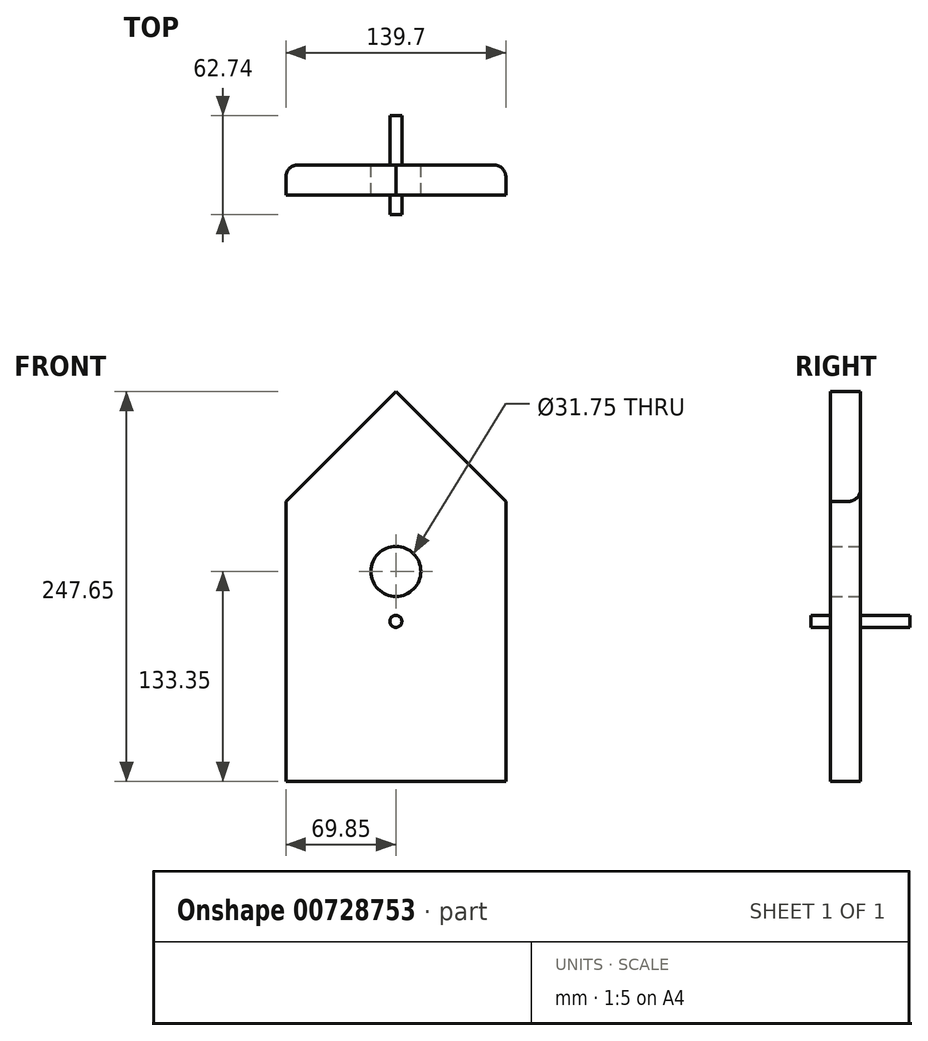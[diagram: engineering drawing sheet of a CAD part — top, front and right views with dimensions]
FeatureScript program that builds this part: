
annotation { "Feature Type Name" : "Feature", "Feature Type Description" : "" }
export const myFeature = defineFeature(function(context is Context, id is Id, definition is map)
    precondition{}
    {
        {
            var Q0;
            Q0=qCreatedBy(makeId("Front.planeOp"),FACE);
            var sketch = newSketch(context, id + "F0", { "sketchPlane" : qUnion([Q0])});
            skLineSegment(sketch, "E0.bottom", {"start": v(69.85, -88.9) * mm, "end": v(-69.85, -88.9) * mm});
            skLineSegment(sketch, "E0.left", {"start": v(69.85, -88.9) * mm, "end": v(69.85, 88.9) * mm});
            skLineSegment(sketch, "E0.right", {"start": v(-69.85, -88.9) * mm, "end": v(-69.85, 88.9) * mm});
            skPoint(sketch, "E0.middle", {"position": v(0, 0) * mm});
            skLineSegment(sketch, "E1", {"start": v(-69.85, 88.9) * mm, "end": v(0, 158.75) * mm});
            skLineSegment(sketch, "E2", {"start": v(0, 158.75) * mm, "end": v(69.85, 88.9) * mm});
            skCircle(sketch, "E3", {"center": v(0, 44.45) * mm, "radius": 15.88 * mm});
            skCircle(sketch, "E4", {"center": v(0, 12.7) * mm, "radius": 3.81 * mm});
            skSolve(sketch);
        }
        {
            var Q0;
            Q0 = qSketchRegion(id + "F0", true);
            extrude(context, id + "F1", {"entities" : qUnion([Q0]), "depth" : 19.05 * mm, "offsetDistance" : 25.4 * mm});
        }
        {
            var Q0;
            Q0=makeQuery(id+"F0.imprint","IMPRINT",FACE,{"disambiguationData":[TD([[makeQuery(id+"F0.imprint","IMPRINT",EDGE,{"derivedFrom":sQuery(id+"F0.wireOp",EDGE,"E4")}),1.0]])]});
            extrude(context, id + "F2", {"entities" : qUnion([Q0]), "operationType" : NewBodyOperationType.ADD, "endBound" : BoundingType.SYMMETRIC, "depth" : 62.74 * mm, "offsetDistance" : 25.4 * mm});
        }
        {
            var Q0;
            Q0=makeQuery(id+"F1.opExtrude","CAP_EDGE",EDGE,{"disambiguationData":[OSD([sQuery(id+"F0.wireOp",EDGE,"E0.left")])],"isStart":true});
            fillet(context, id + "F3", {"entities" : qUnion([Q0]), "radius" : 7.62 * mm, "tangentPropagation" : true, "allowEdgeOverflow" : false});
        }
        {
            var Q0;
            Q0=makeQuery(id+"F1.opExtrude","CAP_EDGE",EDGE,{"disambiguationData":[OSD([sQuery(id+"F0.wireOp",EDGE,"E0.right")])],"isStart":true});
            fillet(context, id + "F4", {"entities" : qUnion([Q0]), "radius" : 7.62 * mm, "tangentPropagation" : true, "allowEdgeOverflow" : false});
        }
    });
